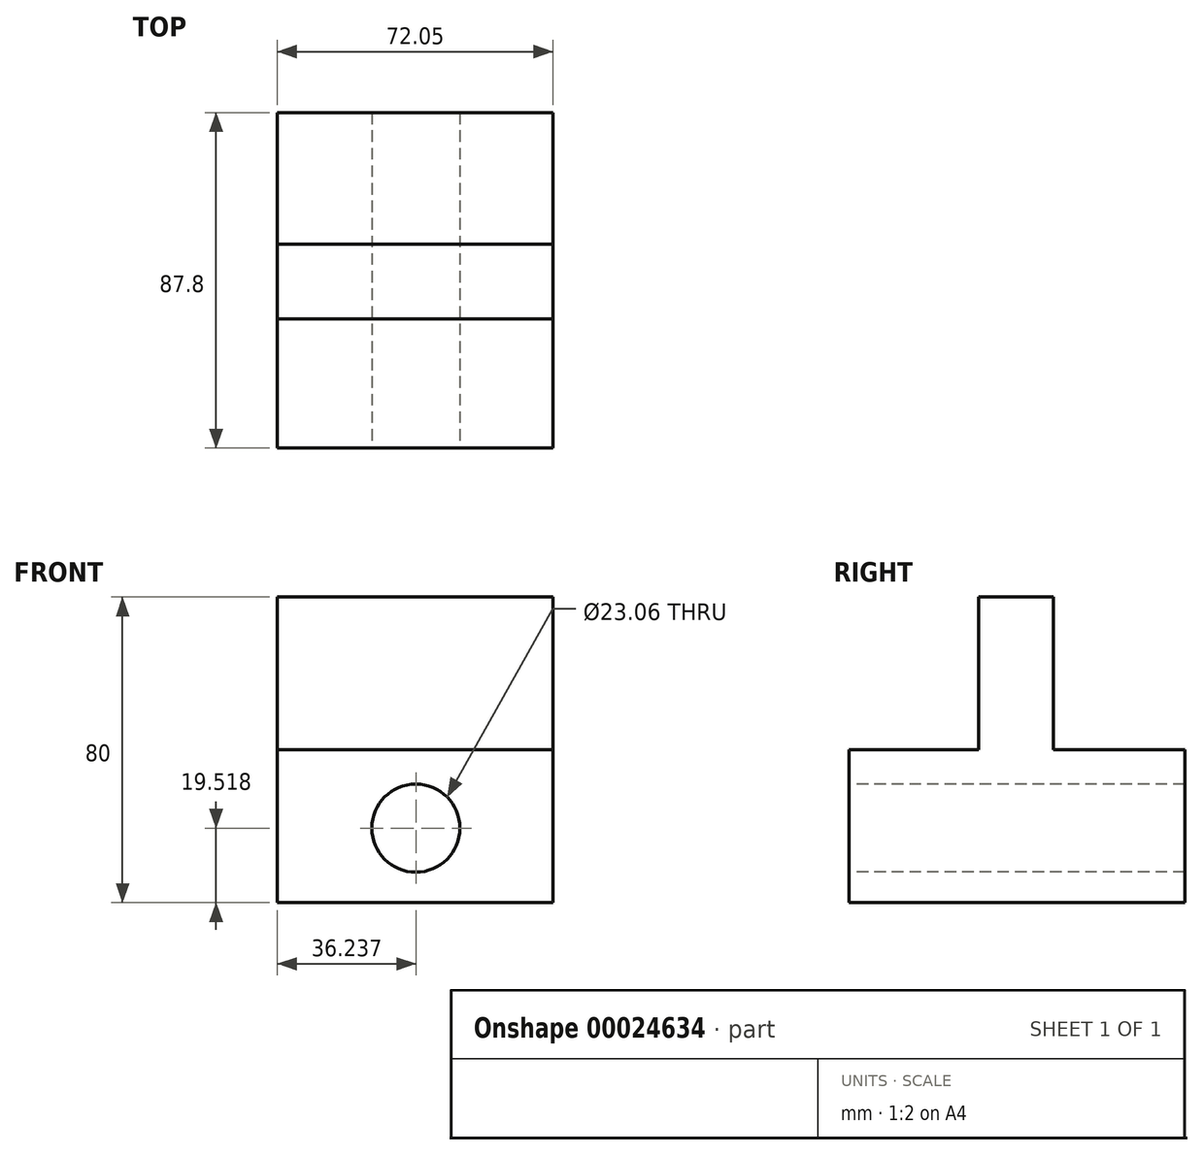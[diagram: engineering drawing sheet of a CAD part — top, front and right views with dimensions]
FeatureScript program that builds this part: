
annotation { "Feature Type Name" : "Feature", "Feature Type Description" : "" }
export const myFeature = defineFeature(function(context is Context, id is Id, definition is map)
    precondition{}
    {
        {
            var Q0;
            Q0=qCreatedBy(makeId("Top.planeOp"),FACE);
            var sketch = newSketch(context, id + "F0", { "sketchPlane" : qUnion([Q0])});
            skLineSegment(sketch, "E0.bottom", {"start": v(-59.89, -44.54) * mm, "end": v(12.16, -44.54) * mm});
            skLineSegment(sketch, "E0.top", {"start": v(-59.89, 43.26) * mm, "end": v(12.16, 43.26) * mm});
            skLineSegment(sketch, "E0.left", {"start": v(-59.89, -44.54) * mm, "end": v(-59.89, 43.26) * mm});
            skLineSegment(sketch, "E0.right", {"start": v(12.16, -44.54) * mm, "end": v(12.16, 43.26) * mm});
            skSolve(sketch);
        }
        {
            var Q0;
            Q0=makeQuery(id+"F0.imprint","IMPRINT",FACE,{"disambiguationData":[TD([[makeQuery(id+"F0.imprint","IMPRINT",EDGE,{"derivedFrom":sQuery(id+"F0.wireOp",EDGE,"E0.bottom")}),1.0]])]});
            extrude(context, id + "F1", {"entities" : qUnion([Q0]), "depth" : 40 * mm});
        }
        {
            var Q0;
            Q0=makeQuery(id+"F1.opExtrude","SWEPT_FACE",FACE,{"disambiguationData":[OSD([sQuery(id+"F0.wireOp",EDGE,"E0.bottom")])]});
            var sketch = newSketch(context, id + "F2", { "sketchPlane" : qUnion([Q0])});
            skCircle(sketch, "E1", {"center": v(-23.65, 19.52) * mm, "radius": 11.53 * mm});
            skSolve(sketch);
        }
        {
            var Q0;
            Q0=makeQuery(id+"F2.imprint","IMPRINT",FACE,{"disambiguationData":[TD([[makeQuery(id+"F2.imprint","IMPRINT",EDGE,{"derivedFrom":sQuery(id+"F2.wireOp",EDGE,"E1")}),1.0]])]});
            extrude(context, id + "F3", {"entities" : qUnion([Q0]), "operationType" : NewBodyOperationType.REMOVE, "endBound" : BoundingType.THROUGH_ALL, "oppositeDirection" : true, "depth" : 25 * mm});
        }
        {
            var Q0;
            Q0=makeQuery(id+"F1.opExtrude","CAP_FACE",FACE,{"disambiguationData":[OSD([sQuery(id+"F0.wireOp",EDGE,"E0.bottom"),sQuery(id+"F0.wireOp",EDGE,"E0.top"),sQuery(id+"F0.wireOp",EDGE,"E0.left"),sQuery(id+"F0.wireOp",EDGE,"E0.right")])],"isStart":false});
            var sketch = newSketch(context, id + "F4", { "sketchPlane" : qUnion([Q0])});
            skLineSegment(sketch, "E2.bottom", {"start": v(-59.89, -10.7) * mm, "end": v(12.16, -10.7) * mm});
            skLineSegment(sketch, "E2.top", {"start": v(-59.89, 8.88) * mm, "end": v(12.16, 8.88) * mm});
            skLineSegment(sketch, "E2.left", {"start": v(-59.89, -10.7) * mm, "end": v(-59.89, 8.88) * mm});
            skLineSegment(sketch, "E2.right", {"start": v(12.16, -10.7) * mm, "end": v(12.16, 8.88) * mm});
            skSolve(sketch);
        }
        {
            var Q0;
            Q0=makeQuery(id+"F4.imprint","IMPRINT",FACE,{"disambiguationData":[TD([[makeQuery(id+"F4.imprint","IMPRINT",EDGE,{"derivedFrom":sQuery(id+"F4.wireOp",EDGE,"E2.bottom")}),1.0]])]});
            extrude(context, id + "F5", {"entities" : qUnion([Q0]), "operationType" : NewBodyOperationType.ADD, "depth" : 40 * mm});
        }
    });
